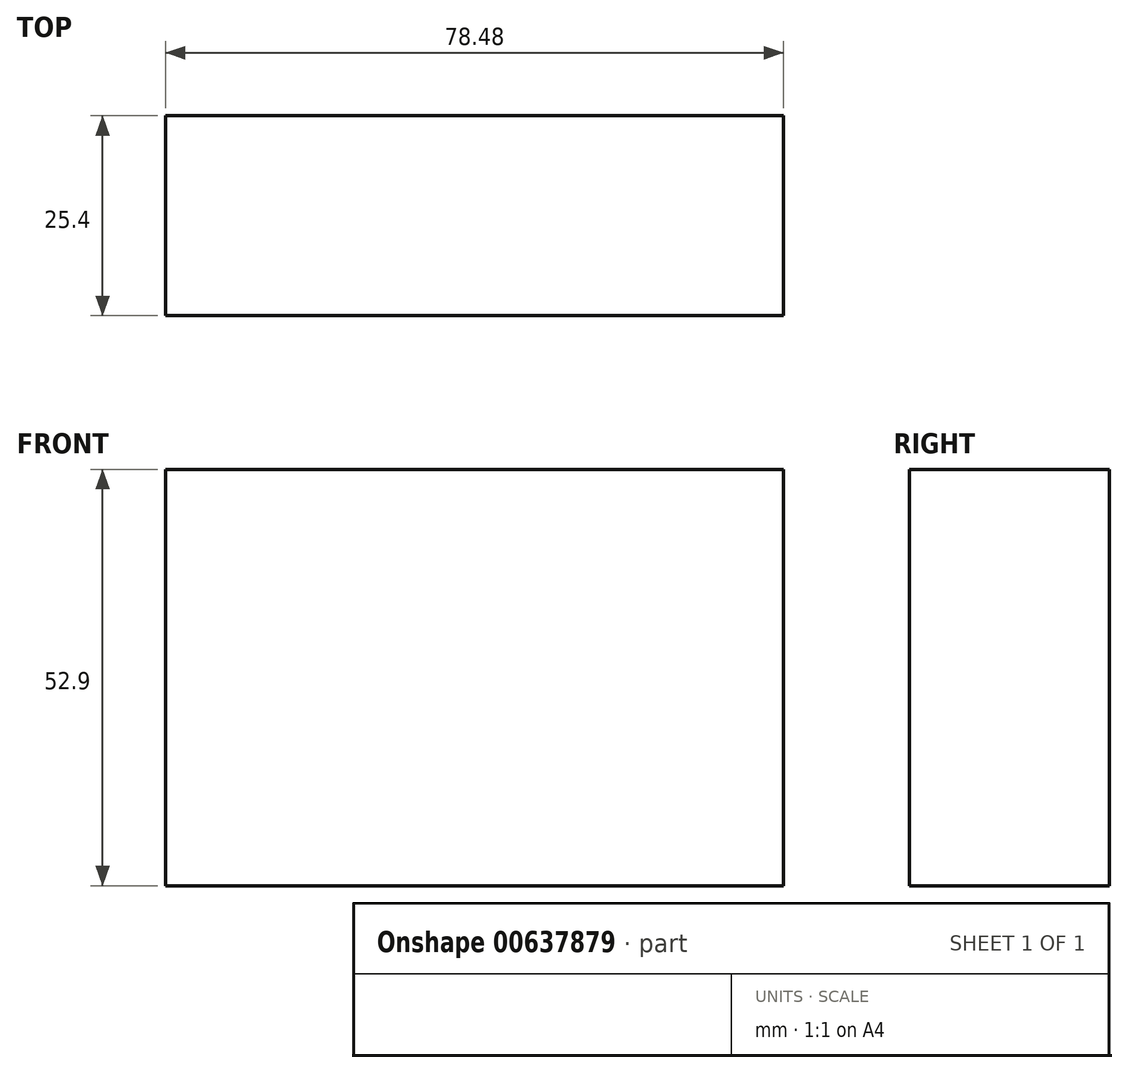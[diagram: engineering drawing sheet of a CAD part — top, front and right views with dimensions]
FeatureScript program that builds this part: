
annotation { "Feature Type Name" : "Feature", "Feature Type Description" : "" }
export const myFeature = defineFeature(function(context is Context, id is Id, definition is map)
    precondition{}
    {
        {
            var Q0;
            Q0=qCreatedBy(makeId("Front.planeOp"),FACE);
            var sketch = newSketch(context, id + "F0", { "sketchPlane" : qUnion([Q0])});
            skLineSegment(sketch, "E0.bottom", {"start": v(-15.37, 26.45) * mm, "end": v(63.11, 26.45) * mm});
            skLineSegment(sketch, "E0.top", {"start": v(-15.37, -26.45) * mm, "end": v(63.11, -26.45) * mm});
            skLineSegment(sketch, "E0.left", {"start": v(-15.37, 26.45) * mm, "end": v(-15.37, -26.45) * mm});
            skLineSegment(sketch, "E0.right", {"start": v(63.11, 26.45) * mm, "end": v(63.11, -26.45) * mm});
            skSolve(sketch);
        }
        {
            var Q0;
            Q0 = qSketchRegion(id + "F0", true);
            extrude(context, id + "F1", {"entities" : qUnion([Q0]), "depth" : 25.4 * mm, "offsetDistance" : 25.4 * mm});
        }
    });
